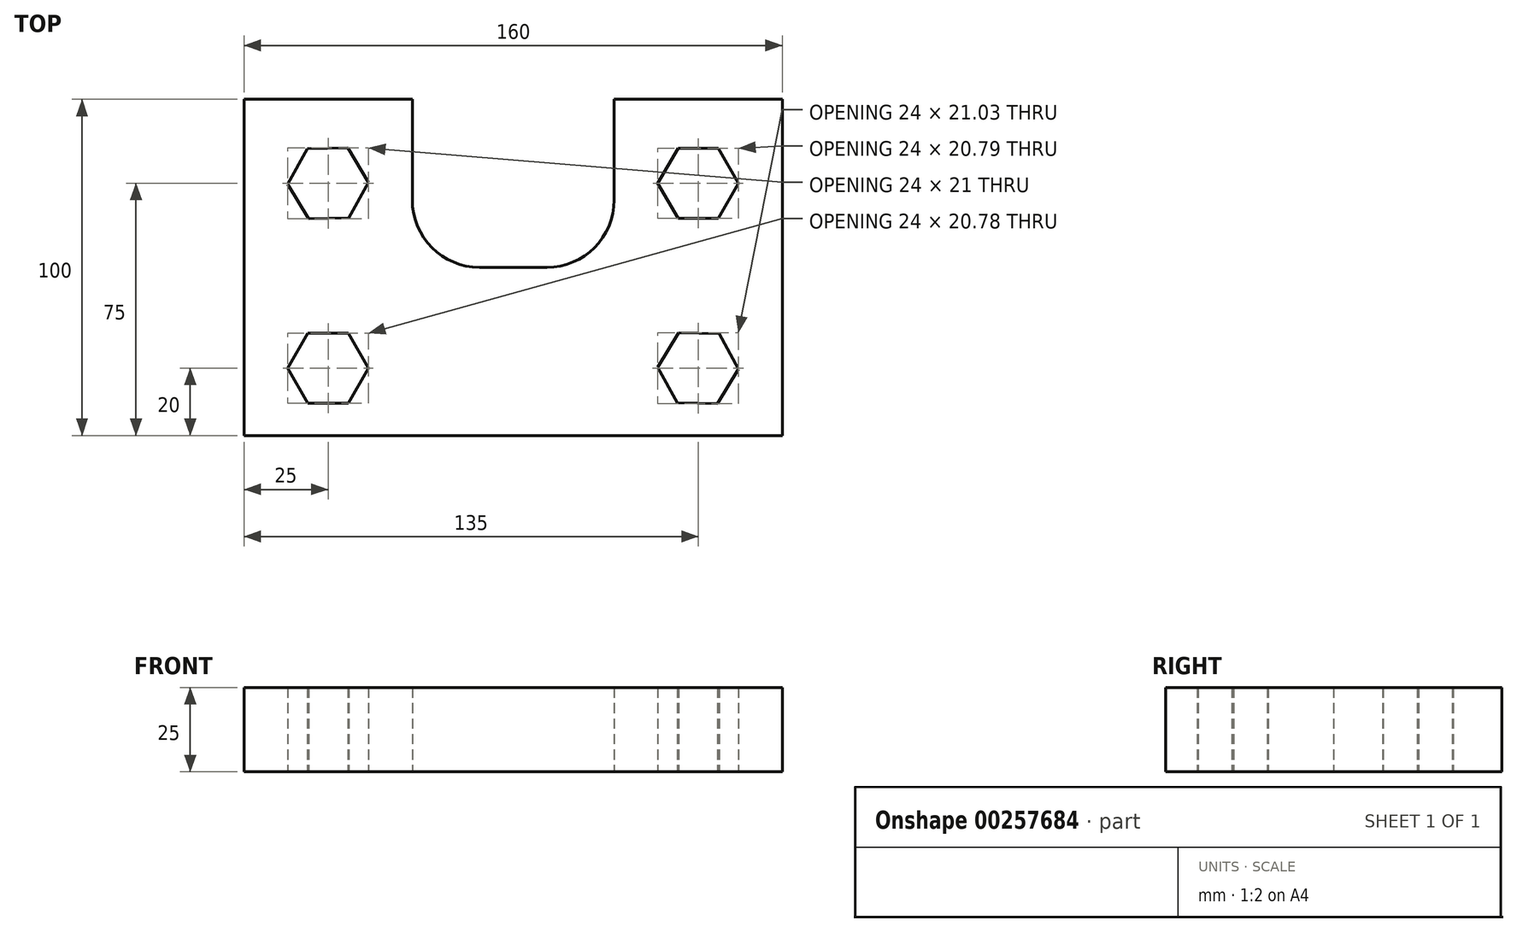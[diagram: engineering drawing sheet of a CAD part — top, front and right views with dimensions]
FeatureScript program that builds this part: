
annotation { "Feature Type Name" : "Feature", "Feature Type Description" : "" }
export const myFeature = defineFeature(function(context is Context, id is Id, definition is map)
    precondition{}
    {
        {
            var Q0;
            Q0=qCreatedBy(makeId("Top.planeOp"),FACE);
            var sketch = newSketch(context, id + "F0", { "sketchPlane" : qUnion([Q0])});
            skLineSegment(sketch, "E0", {"start": v(-67.93, -45.82) * mm, "end": v(92.07, -45.82) * mm});
            skLineSegment(sketch, "E1", {"start": v(92.07, 54.18) * mm, "end": v(42.07, 54.18) * mm});
            skLineSegment(sketch, "E2", {"start": v(42.07, 54.18) * mm, "end": v(42.07, 24.18) * mm});
            skLineSegment(sketch, "E3", {"start": v(22.07, 4.18) * mm, "end": v(2.07, 4.18) * mm});
            skLineSegment(sketch, "E4", {"start": v(-17.93, 24.18) * mm, "end": v(-17.93, 54.18) * mm});
            skLineSegment(sketch, "E5", {"start": v(-17.93, 54.18) * mm, "end": v(-67.93, 54.18) * mm});
            skLineSegment(sketch, "E6", {"start": v(-67.93, 54.18) * mm, "end": v(-67.93, -45.82) * mm});
            skPoint(sketch, "E7.visualSharp", {"position": v(-17.93, 4.18) * mm});
            skArc(sketch, "E7.filletArc", {"start": v(-17.93, 24.18) * mm, "mid": v(-12.07, 10.04) * mm, "end": v(2.07, 4.18) * mm});
            skPoint(sketch, "E8.visualSharp", {"position": v(42.07, 4.18) * mm});
            skArc(sketch, "E8.filletArc", {"start": v(22.07, 4.18) * mm, "mid": v(36.21, 10.04) * mm, "end": v(42.07, 24.18) * mm});
            skLineSegment(sketch, "E9", {"start": v(78.93, -25.82) * mm, "end": v(77.46, -25.82) * mm});
            skLineSegment(sketch, "E10", {"start": v(-67.93, -45.82) * mm, "end": v(-42.93, -45.82) * mm});
            skLineSegment(sketch, "E11", {"start": v(92.07, -45.82) * mm, "end": v(67.07, -45.82) * mm});
            skLineSegment(sketch, "E12", {"start": v(67.07, -36.22) * mm, "end": v(67.07, -36.21) * mm});
            skLineSegment(sketch, "E13", {"start": v(79.07, 29.18) * mm, "end": v(77.46, 29.18) * mm});
            skCircle(sketch, "E14.cCircle", {"center": v(-42.93, -25.82) * mm, "radius": 10.4 * mm, "construction": true});
            skLineSegment(sketch, "E14.0", {"start": v(-36.93, -36.21) * mm, "end": v(-48.93, -36.21) * mm});
            skLineSegment(sketch, "E14.1", {"start": v(-48.93, -36.21) * mm, "end": v(-54.93, -25.82) * mm});
            skLineSegment(sketch, "E14.2", {"start": v(-54.93, -25.82) * mm, "end": v(-48.93, -15.43) * mm});
            skLineSegment(sketch, "E14.3", {"start": v(-48.93, -15.43) * mm, "end": v(-36.93, -15.43) * mm});
            skLineSegment(sketch, "E14.4", {"start": v(-36.93, -15.43) * mm, "end": v(-30.93, -25.82) * mm});
            skLineSegment(sketch, "E14.5", {"start": v(-30.93, -25.82) * mm, "end": v(-36.93, -36.21) * mm});
            skPoint(sketch, "E14.0.midPoint", {"position": v(-42.93, -36.21) * mm});
            skCircle(sketch, "E15.cCircle", {"center": v(-42.93, 29.18) * mm, "radius": 10.4 * mm, "construction": true});
            skLineSegment(sketch, "E15.0", {"start": v(-48.75, 18.68) * mm, "end": v(-54.93, 28.97) * mm});
            skLineSegment(sketch, "E15.1", {"start": v(-54.93, 28.97) * mm, "end": v(-49.11, 39.47) * mm});
            skLineSegment(sketch, "E15.2", {"start": v(-49.11, 39.47) * mm, "end": v(-37.11, 39.68) * mm});
            skLineSegment(sketch, "E15.3", {"start": v(-37.11, 39.68) * mm, "end": v(-30.93, 29.4) * mm});
            skLineSegment(sketch, "E15.4", {"start": v(-30.93, 29.4) * mm, "end": v(-36.75, 18.9) * mm});
            skLineSegment(sketch, "E15.5", {"start": v(-36.75, 18.9) * mm, "end": v(-48.75, 18.68) * mm});
            skPoint(sketch, "E15.0.midPoint", {"position": v(-51.84, 23.82) * mm});
            skCircle(sketch, "E16.cCircle", {"center": v(67.07, 29.18) * mm, "radius": 10.4 * mm, "construction": true});
            skLineSegment(sketch, "E16.0", {"start": v(61.08, 18.78) * mm, "end": v(55.07, 29.17) * mm});
            skLineSegment(sketch, "E16.1", {"start": v(55.07, 29.17) * mm, "end": v(61.06, 39.57) * mm});
            skLineSegment(sketch, "E16.2", {"start": v(61.06, 39.57) * mm, "end": v(73.06, 39.58) * mm});
            skLineSegment(sketch, "E16.3", {"start": v(73.06, 39.58) * mm, "end": v(79.07, 29.19) * mm});
            skLineSegment(sketch, "E16.4", {"start": v(79.07, 29.19) * mm, "end": v(73.08, 18.8) * mm});
            skLineSegment(sketch, "E16.5", {"start": v(73.08, 18.8) * mm, "end": v(61.08, 18.78) * mm});
            skPoint(sketch, "E16.0.midPoint", {"position": v(58.07, 23.98) * mm});
            skCircle(sketch, "E17.cCircle", {"center": v(67.07, -25.82) * mm, "radius": 10.4 * mm, "construction": true});
            skLineSegment(sketch, "E17.0", {"start": v(60.86, -36.09) * mm, "end": v(55.07, -25.57) * mm});
            skLineSegment(sketch, "E17.1", {"start": v(55.07, -25.57) * mm, "end": v(61.28, -15.3) * mm});
            skLineSegment(sketch, "E17.2", {"start": v(61.28, -15.3) * mm, "end": v(73.28, -15.55) * mm});
            skLineSegment(sketch, "E17.3", {"start": v(73.28, -15.55) * mm, "end": v(79.07, -26.07) * mm});
            skLineSegment(sketch, "E17.4", {"start": v(79.07, -26.07) * mm, "end": v(72.86, -36.34) * mm});
            skLineSegment(sketch, "E17.5", {"start": v(72.86, -36.34) * mm, "end": v(60.86, -36.09) * mm});
            skPoint(sketch, "E17.0.midPoint", {"position": v(57.96, -30.83) * mm});
            skPoint(sketch, "E18.orphan", {"position": v(-42.93, 54.18) * mm});
            skLineSegment(sketch, "E19.trimOffspring", {"start": v(-42.93, 39.57) * mm, "end": v(-42.93, 39.58) * mm});
            skLineSegment(sketch, "E20.trimOffspring", {"start": v(-53.32, 29.18) * mm, "end": v(-54.81, 29.18) * mm});
            skLineSegment(sketch, "E21.trimOffspring", {"start": v(-42.93, 18.78) * mm, "end": v(-42.93, 18.79) * mm});
            skLineSegment(sketch, "E22.trimOffspring", {"start": v(-53.32, -25.82) * mm, "end": v(-54.93, -25.82) * mm});
            skLineSegment(sketch, "E23.trimOffspring", {"start": v(-30.93, -25.82) * mm, "end": v(-32.54, -25.82) * mm});
            skLineSegment(sketch, "E24.trimOffspring", {"start": v(56.68, -25.82) * mm, "end": v(55.2, -25.82) * mm});
            skLineSegment(sketch, "E25.trimOffspring", {"start": v(67.07, -15.43) * mm, "end": v(67.07, -15.42) * mm});
            skPoint(sketch, "E26.trimOffspring.end.orphan", {"position": v(67.07, 54.18) * mm});
            skLineSegment(sketch, "E27.trimOffspring", {"start": v(56.68, 29.18) * mm, "end": v(55.07, 29.18) * mm});
            skLineSegment(sketch, "E28.trimOffspring", {"start": v(-31.05, 29.18) * mm, "end": v(-32.54, 29.18) * mm});
            skLineSegment(sketch, "E29", {"start": v(92.07, -45.82) * mm, "end": v(92.07, 54.18) * mm});
            skSolve(sketch);
        }
        {
            var Q0;
            Q0 = qSketchRegion(id + "F0", true);
            extrude(context, id + "F1", {"entities" : qUnion([Q0]), "depth" : 25 * mm});
        }
    });
